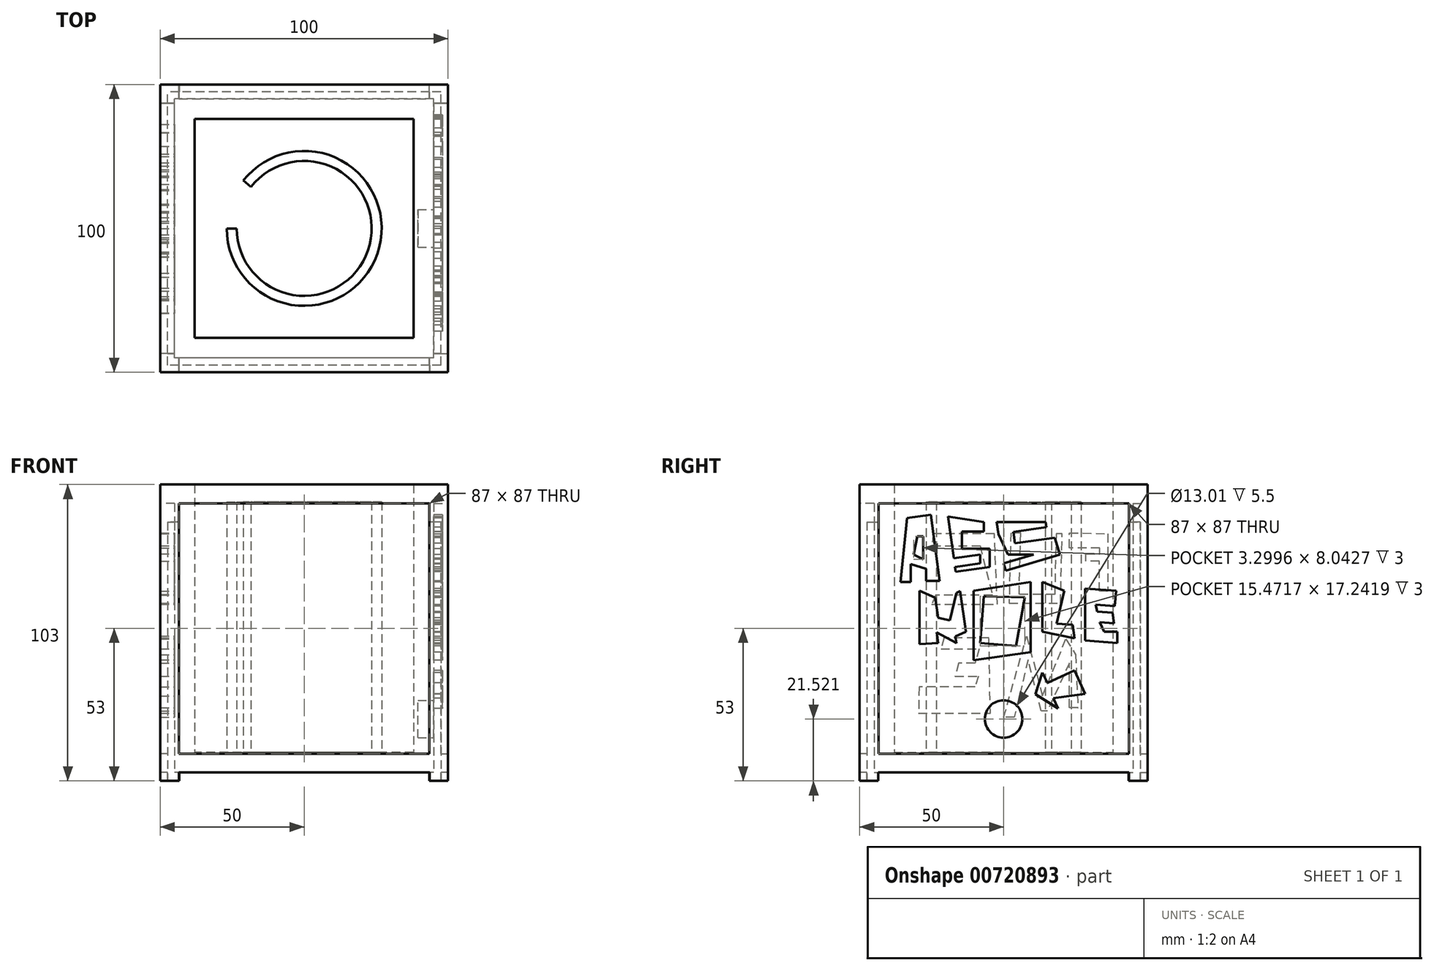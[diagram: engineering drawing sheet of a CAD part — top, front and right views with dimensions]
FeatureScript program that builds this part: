
annotation { "Feature Type Name" : "Feature", "Feature Type Description" : "" }
export const myFeature = defineFeature(function(context is Context, id is Id, definition is map)
    precondition{}
    {
        {
            var Q0;
            Q0=qCreatedBy(makeId("Top.planeOp"),FACE);
            var sketch = newSketch(context, id + "F0", { "sketchPlane" : qUnion([Q0])});
            skLineSegment(sketch, "E0.bottom", {"start": v(50, 50) * mm, "end": v(-50, 50) * mm});
            skLineSegment(sketch, "E0.top", {"start": v(50, -50) * mm, "end": v(-50, -50) * mm});
            skLineSegment(sketch, "E0.left", {"start": v(50, 50) * mm, "end": v(50, -50) * mm});
            skLineSegment(sketch, "E0.right", {"start": v(-50, 50) * mm, "end": v(-50, -50) * mm});
            skPoint(sketch, "E0.middle", {"position": v(0, 0) * mm});
            skSolve(sketch);
        }
        {
            var Q0;
            Q0=makeQuery(id+"F0.imprint","IMPRINT",FACE,{"disambiguationData":[TD([[makeQuery(id+"F0.imprint","IMPRINT",EDGE,{"derivedFrom":sQuery(id+"F0.wireOp",EDGE,"E0.bottom")}),1.0]])]});
            extrude(context, id + "F1", {"entities" : qUnion([Q0]), "depth" : 100 * mm, "offsetDistance" : 25 * mm});
        }
        {
            var Q0;
            Q0=makeQuery(id+"F1.opExtrude","CAP_FACE",FACE,{"disambiguationData":[OSD([sQuery(id+"F0.wireOp",EDGE,"E0.bottom"),sQuery(id+"F0.wireOp",EDGE,"E0.top"),sQuery(id+"F0.wireOp",EDGE,"E0.left"),sQuery(id+"F0.wireOp",EDGE,"E0.right")])],"isStart":true});
            var sketch = newSketch(context, id + "F2", { "sketchPlane" : qUnion([Q0])});
            skLineSegment(sketch, "E1.bottom", {"start": v(47.5, 47.5) * mm, "end": v(-47.5, 47.5) * mm});
            skLineSegment(sketch, "E1.top", {"start": v(47.5, -47.5) * mm, "end": v(-47.5, -47.5) * mm});
            skLineSegment(sketch, "E1.left", {"start": v(47.5, 47.5) * mm, "end": v(47.5, -47.5) * mm});
            skLineSegment(sketch, "E1.right", {"start": v(-47.5, 47.5) * mm, "end": v(-47.5, -47.5) * mm});
            skPoint(sketch, "E1.middle", {"position": v(0, 0) * mm});
            skLineSegment(sketch, "E2.bottom", {"start": v(45, 45) * mm, "end": v(-45, 45) * mm});
            skLineSegment(sketch, "E2.top", {"start": v(45, -45) * mm, "end": v(-45, -45) * mm});
            skLineSegment(sketch, "E2.left", {"start": v(45, 45) * mm, "end": v(45, -45) * mm});
            skLineSegment(sketch, "E2.right", {"start": v(-45, 45) * mm, "end": v(-45, -45) * mm});
            skSolve(sketch);
        }
        {
            var Q0;
            Q0=makeQuery(id+"F2.imprint","IMPRINT",FACE,{"disambiguationData":[TD([[makeQuery(id+"F2.imprint","IMPRINT",EDGE,{"derivedFrom":sQuery(id+"F2.wireOp",EDGE,"E1.bottom")}),1.0]])]});
            extrude(context, id + "F3", {"entities" : qUnion([Q0]), "operationType" : NewBodyOperationType.REMOVE, "oppositeDirection" : true, "depth" : 87 * mm, "offsetDistance" : 25 * mm});
        }
        {
            var Q0;
            Q0=makeQuery(id+"F1.opExtrude","CAP_FACE",FACE,{"disambiguationData":[OSD([sQuery(id+"F0.wireOp",EDGE,"E0.bottom"),sQuery(id+"F0.wireOp",EDGE,"E0.top"),sQuery(id+"F0.wireOp",EDGE,"E0.left"),sQuery(id+"F0.wireOp",EDGE,"E0.right")])],"isStart":false});
            shell(context, id + "F4", {"entities" : qUnion([Q0]), "thickness" : 7 * mm});
        }
        {
            var Q0;
            Q0=makeQuery(id+"F1.opExtrude","SWEPT_FACE",FACE,{"disambiguationData":[OSD([sQuery(id+"F0.wireOp",EDGE,"E0.right")])]});
            var sketch = newSketch(context, id + "F5", { "sketchPlane" : qUnion([Q0])});
            skLineSegment(sketch, "E3", {"start": v(0, 0) * mm, "end": v(0, 102.86) * mm, "construction": true});
            skLineSegment(sketch, "E4", {"start": v(-50, 50) * mm, "end": v(50, 50) * mm, "construction": true});
            skLineSegment(sketch, "E5.bottom", {"start": v(43.5, 93.5) * mm, "end": v(-43.5, 93.5) * mm});
            skLineSegment(sketch, "E5.top", {"start": v(43.5, 6.5) * mm, "end": v(-43.5, 6.5) * mm});
            skLineSegment(sketch, "E5.left", {"start": v(43.5, 93.5) * mm, "end": v(43.5, 6.5) * mm});
            skLineSegment(sketch, "E5.right", {"start": v(-43.5, 93.5) * mm, "end": v(-43.5, 6.5) * mm});
            skPoint(sketch, "E5.middle", {"position": v(0, 50) * mm});
            skSolve(sketch);
        }
        {
            var Q0;
            Q0=makeQuery(id+"F1.opExtrude","SWEPT_FACE",FACE,{"disambiguationData":[OSD([sQuery(id+"F0.wireOp",EDGE,"E0.top")])]});
            var sketch = newSketch(context, id + "F6", { "sketchPlane" : qUnion([Q0])});
            skLineSegment(sketch, "E6", {"start": v(-50, 50) * mm, "end": v(50, 50) * mm, "construction": true});
            skLineSegment(sketch, "E7", {"start": v(0, 0) * mm, "end": v(0, 100) * mm, "construction": true});
            skLineSegment(sketch, "E8.bottom", {"start": v(43.5, 93.5) * mm, "end": v(-43.5, 93.5) * mm});
            skLineSegment(sketch, "E8.top", {"start": v(43.5, 6.5) * mm, "end": v(-43.5, 6.5) * mm});
            skLineSegment(sketch, "E8.left", {"start": v(43.5, 93.5) * mm, "end": v(43.5, 6.5) * mm});
            skLineSegment(sketch, "E8.right", {"start": v(-43.5, 93.5) * mm, "end": v(-43.5, 6.5) * mm});
            skPoint(sketch, "E8.middle", {"position": v(0, 50) * mm});
            skSolve(sketch);
        }
        {
            var Q0;
            Q0=makeQuery(id+"F1.opExtrude","SWEPT_FACE",FACE,{"disambiguationData":[OSD([sQuery(id+"F0.wireOp",EDGE,"E0.left")])]});
            var sketch = newSketch(context, id + "F7", { "sketchPlane" : qUnion([Q0])});
            skLineSegment(sketch, "E9", {"start": v(-50, 50) * mm, "end": v(50, 50) * mm, "construction": true});
            skLineSegment(sketch, "E10", {"start": v(0, 100) * mm, "end": v(0, 0) * mm, "construction": true});
            skLineSegment(sketch, "E11.bottom", {"start": v(43.5, 93.5) * mm, "end": v(-43.5, 93.5) * mm});
            skLineSegment(sketch, "E11.top", {"start": v(43.5, 6.5) * mm, "end": v(-43.5, 6.5) * mm});
            skLineSegment(sketch, "E11.left", {"start": v(43.5, 93.5) * mm, "end": v(43.5, 6.5) * mm});
            skLineSegment(sketch, "E11.right", {"start": v(-43.5, 93.5) * mm, "end": v(-43.5, 6.5) * mm});
            skPoint(sketch, "E11.middle", {"position": v(0, 50) * mm});
            skSolve(sketch);
        }
        {
            var Q0;
            Q0=makeQuery(id+"F1.opExtrude","SWEPT_FACE",FACE,{"disambiguationData":[OSD([sQuery(id+"F0.wireOp",EDGE,"E0.bottom")])]});
            var sketch = newSketch(context, id + "F8", { "sketchPlane" : qUnion([Q0])});
            skLineSegment(sketch, "E12", {"start": v(-50, 50) * mm, "end": v(50, 50) * mm, "construction": true});
            skLineSegment(sketch, "E13", {"start": v(0, 100) * mm, "end": v(0, 0) * mm, "construction": true});
            skLineSegment(sketch, "E14.bottom", {"start": v(43.5, 93.5) * mm, "end": v(-43.5, 93.5) * mm});
            skLineSegment(sketch, "E14.top", {"start": v(43.5, 6.5) * mm, "end": v(-43.5, 6.5) * mm});
            skLineSegment(sketch, "E14.left", {"start": v(43.5, 93.5) * mm, "end": v(43.5, 6.5) * mm});
            skLineSegment(sketch, "E14.right", {"start": v(-43.5, 93.5) * mm, "end": v(-43.5, 6.5) * mm});
            skPoint(sketch, "E14.middle", {"position": v(0, 50) * mm});
            skSolve(sketch);
        }
        {
            var Q0;
            Q0=makeQuery(id+"F5.imprint","IMPRINT",FACE,{"disambiguationData":[TD([[makeQuery(id+"F5.imprint","IMPRINT",EDGE,{"derivedFrom":sQuery(id+"F5.wireOp",EDGE,"E5.bottom")}),1.0]])]});
            extrude(context, id + "F9", {"entities" : qUnion([Q0]), "operationType" : NewBodyOperationType.REMOVE, "oppositeDirection" : true, "depth" : 5 * mm, "offsetDistance" : 25 * mm});
        }
        {
            var Q0;
            Q0=makeQuery(id+"F7.imprint","IMPRINT",FACE,{"disambiguationData":[TD([[makeQuery(id+"F7.imprint","IMPRINT",EDGE,{"derivedFrom":sQuery(id+"F7.wireOp",EDGE,"E11.bottom")}),1.0]])]});
            extrude(context, id + "F10", {"entities" : qUnion([Q0]), "operationType" : NewBodyOperationType.REMOVE, "oppositeDirection" : true, "depth" : 5 * mm, "offsetDistance" : 25 * mm});
        }
        {
            var Q0;
            Q0=makeQuery(id+"F8.imprint","IMPRINT",FACE,{"disambiguationData":[TD([[makeQuery(id+"F8.imprint","IMPRINT",EDGE,{"derivedFrom":sQuery(id+"F8.wireOp",EDGE,"E14.bottom")}),1.0]])]});
            extrude(context, id + "F11", {"entities" : qUnion([Q0]), "operationType" : NewBodyOperationType.REMOVE, "oppositeDirection" : true, "depth" : 5 * mm, "offsetDistance" : 25 * mm});
        }
        {
            var Q0;
            Q0=makeQuery(id+"F6.imprint","IMPRINT",FACE,{"disambiguationData":[TD([[makeQuery(id+"F6.imprint","IMPRINT",EDGE,{"derivedFrom":sQuery(id+"F6.wireOp",EDGE,"E8.bottom")}),1.0]])]});
            extrude(context, id + "F12", {"entities" : qUnion([Q0]), "operationType" : NewBodyOperationType.REMOVE, "oppositeDirection" : true, "depth" : 5 * mm, "offsetDistance" : 25 * mm});
        }
        {
            var Q0;
            {var subQ0=sQuery(id+"F0.wireOp",EDGE,"E0.left");var subQ1=sQuery(id+"F0.wireOp",EDGE,"E0.top");var subQ2=sQuery(id+"F0.wireOp",EDGE,"E0.right");var subQ3=sQuery(id+"F0.wireOp",EDGE,"E0.bottom");Q0=makeQuery(id+"F3.boolean.opBoolean","SPLIT",FACE,{"disambiguationData":[TD([makeQuery(id+"F1.opExtrude","SWEPT_FACE",FACE,{"disambiguationData":[OSD([subQ3])]})])],"derivedFrom":makeQuery(id+"F1.opExtrude","CAP_FACE",FACE,{"disambiguationData":[OSD([subQ3,subQ1,subQ0,subQ2])],"isStart":true})});}
            var sketch = newSketch(context, id + "F13", { "sketchPlane" : qUnion([Q0])});
            skLineSegment(sketch, "E15", {"start": v(-47.5, 43.53) * mm, "end": v(-50, 43.53) * mm});
            skLineSegment(sketch, "E16", {"start": v(-50, 43.53) * mm, "end": v(-50, 50) * mm});
            skLineSegment(sketch, "E17", {"start": v(-50, 50) * mm, "end": v(-43.53, 50) * mm});
            skLineSegment(sketch, "E18", {"start": v(-43.53, 50) * mm, "end": v(-43.53, 47.5) * mm});
            skLineSegment(sketch, "E19", {"start": v(-43.53, 47.5) * mm, "end": v(-47.5, 47.5) * mm});
            skLineSegment(sketch, "E20", {"start": v(-47.5, 47.5) * mm, "end": v(-47.5, 43.53) * mm});
            skLineSegment(sketch, "E21", {"start": v(-47.5, -43.38) * mm, "end": v(-50, -43.38) * mm});
            skLineSegment(sketch, "E22", {"start": v(-50, -43.38) * mm, "end": v(-50, -50) * mm});
            skLineSegment(sketch, "E23", {"start": v(-50, -50) * mm, "end": v(-43.38, -50) * mm});
            skLineSegment(sketch, "E24", {"start": v(-43.38, -50) * mm, "end": v(-43.38, -47.5) * mm});
            skLineSegment(sketch, "E25", {"start": v(-43.38, -47.5) * mm, "end": v(-47.5, -47.5) * mm});
            skLineSegment(sketch, "E26", {"start": v(-47.5, -47.5) * mm, "end": v(-47.5, -43.38) * mm});
            skLineSegment(sketch, "E27", {"start": v(43.51, -47.5) * mm, "end": v(43.51, -50) * mm});
            skLineSegment(sketch, "E28", {"start": v(43.51, -50) * mm, "end": v(50, -50) * mm});
            skLineSegment(sketch, "E29", {"start": v(50, -50) * mm, "end": v(50, -43.51) * mm});
            skLineSegment(sketch, "E30", {"start": v(50, -43.51) * mm, "end": v(47.5, -43.51) * mm});
            skLineSegment(sketch, "E31", {"start": v(47.5, -43.51) * mm, "end": v(47.5, -47.5) * mm});
            skLineSegment(sketch, "E32", {"start": v(47.5, -47.5) * mm, "end": v(43.51, -47.5) * mm});
            skLineSegment(sketch, "E33", {"start": v(43.58, 47.5) * mm, "end": v(43.58, 50) * mm});
            skLineSegment(sketch, "E34", {"start": v(43.58, 50) * mm, "end": v(50, 50) * mm});
            skLineSegment(sketch, "E35", {"start": v(50, 50) * mm, "end": v(50, 43.58) * mm});
            skLineSegment(sketch, "E36", {"start": v(50, 43.58) * mm, "end": v(47.5, 43.58) * mm});
            skLineSegment(sketch, "E37", {"start": v(47.5, 43.58) * mm, "end": v(47.5, 47.5) * mm});
            skLineSegment(sketch, "E38", {"start": v(47.5, 47.5) * mm, "end": v(43.58, 47.5) * mm});
            skSolve(sketch);
        }
        {
            var Q0;
            Q0=makeQuery(id+"F13.imprint","IMPRINT",FACE,{"disambiguationData":[TD([[makeQuery(id+"F13.imprint","IMPRINT",EDGE,{"derivedFrom":sQuery(id+"F13.wireOp",EDGE,"E27")}),1.0]])]});
            var Q1;
            Q1=makeQuery(id+"F13.imprint","IMPRINT",FACE,{"disambiguationData":[TD([[makeQuery(id+"F13.imprint","IMPRINT",EDGE,{"derivedFrom":sQuery(id+"F13.wireOp",EDGE,"E21")}),1.0]])]});
            var Q2;
            Q2=makeQuery(id+"F13.imprint","IMPRINT",FACE,{"disambiguationData":[TD([[makeQuery(id+"F13.imprint","IMPRINT",EDGE,{"derivedFrom":sQuery(id+"F13.wireOp",EDGE,"E15")}),-1.0]])]});
            var Q3;
            Q3=makeQuery(id+"F13.imprint","IMPRINT",FACE,{"disambiguationData":[TD([[makeQuery(id+"F13.imprint","IMPRINT",EDGE,{"derivedFrom":sQuery(id+"F13.wireOp",EDGE,"E33")}),-1.0]])]});
            extrude(context, id + "F14", {"entities" : qUnion([Q0, Q1, Q2, Q3]), "operationType" : NewBodyOperationType.ADD, "depth" : 3 * mm, "offsetDistance" : 25 * mm});
        }
        {
            var Q0;
            Q0=makeQuery(id+"F4.opShell","OFFSET_FACE",FACE,{"disambiguationData":[OSD([sQuery(id+"F0.wireOp",EDGE,"E0.bottom"),sQuery(id+"F0.wireOp",EDGE,"E0.top"),sQuery(id+"F0.wireOp",EDGE,"E0.left"),sQuery(id+"F0.wireOp",EDGE,"E0.right")])]});
            var sketch = newSketch(context, id + "F15", { "sketchPlane" : qUnion([Q0])});
            skArc(sketch, "E39", {"start": v(-23.44, 0) * mm, "mid": v(22.16, -7.63) * mm, "end": v(-18.47, 14.42) * mm});
            skLineSegment(sketch, "E40", {"start": v(-26.91, 0) * mm, "end": v(-23.44, 0) * mm});
            skLineSegment(sketch, "E41", {"start": v(-21.13, 16.67) * mm, "end": v(-18.47, 14.42) * mm});
            skArc(sketch, "E42", {"start": v(-21.13, 16.67) * mm, "mid": v(25.42, -8.82) * mm, "end": v(-26.91, 0) * mm});
            skSolve(sketch);
        }
        {
            var Q0;
            Q0 = qSketchRegion(id + "F15", true);
            extrude(context, id + "F16", {"entities" : qUnion([Q0]), "operationType" : NewBodyOperationType.ADD, "depth" : 87 * mm, "offsetDistance" : 25 * mm});
        }
        {
            var Q0;
            Q0=makeQuery(id+"F4.opShell","OFFSET_FACE",FACE,{"disambiguationData":[OSD([sQuery(id+"F2.wireOp",EDGE,"E1.bottom"),sQuery(id+"F2.wireOp",EDGE,"E1.top"),sQuery(id+"F2.wireOp",EDGE,"E1.left"),sQuery(id+"F2.wireOp",EDGE,"E1.right"),sQuery(id+"F2.wireOp",EDGE,"E2.bottom"),sQuery(id+"F2.wireOp",EDGE,"E2.top"),sQuery(id+"F2.wireOp",EDGE,"E2.left"),sQuery(id+"F2.wireOp",EDGE,"E2.right")])]});
            extrude(context, id + "F17", {"entities" : qUnion([Q0]), "operationType" : NewBodyOperationType.ADD, "depth" : 6 * mm, "offsetDistance" : 25 * mm});
        }
        {
            var Q0;
            Q0=makeQuery(id+"F9.boolean.opBoolean","MERGE",FACE,{"derivedFrom":[makeQuery(id+"F3.boolean.opBoolean","COPY",FACE,{"derivedFrom":makeQuery(id+"F3.opExtrude","SWEPT_FACE",FACE,{"disambiguationData":[OSD([sQuery(id+"F2.wireOp",EDGE,"E2.right")])]})}),makeQuery(id+"F9.opExtrude","CAP_FACE",FACE,{"disambiguationData":[OSD([sQuery(id+"F5.wireOp",EDGE,"E5.bottom"),sQuery(id+"F5.wireOp",EDGE,"E5.top"),sQuery(id+"F5.wireOp",EDGE,"E5.left"),sQuery(id+"F5.wireOp",EDGE,"E5.right")])],"isStart":false})]});
            var sketch = newSketch(context, id + "F18", { "sketchPlane" : qUnion([Q0])});
            skLineSegment(sketch, "E43", {"start": v(-36.15, 82.9) * mm, "end": v(-36.15, 62.97) * mm});
            skLineSegment(sketch, "E44", {"start": v(-36.15, 62.97) * mm, "end": v(-33.22, 62.97) * mm});
            skLineSegment(sketch, "E45", {"start": v(-33.22, 62.97) * mm, "end": v(-33.22, 73.32) * mm});
            skLineSegment(sketch, "E46", {"start": v(-33.22, 73.32) * mm, "end": v(-28.58, 73.32) * mm});
            skLineSegment(sketch, "E47", {"start": v(-28.58, 73.32) * mm, "end": v(-28.58, 75.95) * mm});
            skLineSegment(sketch, "E48", {"start": v(-28.58, 75.95) * mm, "end": v(-33.37, 75.95) * mm});
            skLineSegment(sketch, "E49", {"start": v(-33.37, 75.95) * mm, "end": v(-33.37, 77.96) * mm});
            skLineSegment(sketch, "E50", {"start": v(-33.37, 77.96) * mm, "end": v(-22.86, 77.96) * mm});
            skLineSegment(sketch, "E51", {"start": v(-22.86, 77.96) * mm, "end": v(-22.86, 83.21) * mm});
            skLineSegment(sketch, "E52", {"start": v(-22.86, 83.21) * mm, "end": v(-36.15, 82.9) * mm});
            skLineSegment(sketch, "E53", {"start": v(-18.23, 82.9) * mm, "end": v(-17.74, 61.88) * mm});
            skLineSegment(sketch, "E54", {"start": v(-17.74, 61.88) * mm, "end": v(-5.4, 61.88) * mm});
            skLineSegment(sketch, "E55", {"start": v(-5.4, 61.88) * mm, "end": v(-5.9, 83.21) * mm});
            skLineSegment(sketch, "E56", {"start": v(-5.9, 83.21) * mm, "end": v(-2.47, 83.21) * mm});
            skLineSegment(sketch, "E57", {"start": v(-2.47, 83.21) * mm, "end": v(-1.9, 58.82) * mm});
            skLineSegment(sketch, "E58", {"start": v(-1.9, 58.82) * mm, "end": v(-19.77, 58.82) * mm});
            skLineSegment(sketch, "E59", {"start": v(-19.77, 58.82) * mm, "end": v(-20.34, 82.9) * mm});
            skLineSegment(sketch, "E60", {"start": v(-20.34, 82.9) * mm, "end": v(-18.23, 82.9) * mm});
            skLineSegment(sketch, "E61", {"start": v(3.24, 82.9) * mm, "end": v(24.4, 82.9) * mm});
            skLineSegment(sketch, "E62", {"start": v(24.4, 82.9) * mm, "end": v(24.87, 78.73) * mm});
            skLineSegment(sketch, "E63", {"start": v(24.87, 78.73) * mm, "end": v(8.19, 78.73) * mm});
            skLineSegment(sketch, "E64", {"start": v(8.19, 78.73) * mm, "end": v(3.86, 61.58) * mm});
            skLineSegment(sketch, "E65", {"start": v(3.86, 61.58) * mm, "end": v(23.64, 61.58) * mm});
            skLineSegment(sketch, "E66", {"start": v(23.64, 61.58) * mm, "end": v(25.03, 58.34) * mm});
            skLineSegment(sketch, "E67", {"start": v(25.03, 58.34) * mm, "end": v(2.16, 58.34) * mm});
            skLineSegment(sketch, "E68", {"start": v(2.16, 58.34) * mm, "end": v(3.24, 82.9) * mm});
            skLineSegment(sketch, "E69", {"start": v(-25.03, 40.88) * mm, "end": v(-25.84, 22.47) * mm});
            skLineSegment(sketch, "E70", {"start": v(-25.84, 22.47) * mm, "end": v(-22.86, 22.47) * mm});
            skLineSegment(sketch, "E71", {"start": v(-22.86, 22.47) * mm, "end": v(-22.86, 37.94) * mm});
            skLineSegment(sketch, "E72", {"start": v(-22.86, 37.94) * mm, "end": v(-15.3, 21.26) * mm});
            skLineSegment(sketch, "E73", {"start": v(-15.3, 21.26) * mm, "end": v(-13.13, 21.26) * mm});
            skLineSegment(sketch, "E74", {"start": v(-13.13, 21.26) * mm, "end": v(-8.5, 39.03) * mm});
            skLineSegment(sketch, "E75", {"start": v(-8.5, 39.03) * mm, "end": v(-3.7, 19.1) * mm});
            skLineSegment(sketch, "E76", {"start": v(-3.7, 19.1) * mm, "end": v(0, 19.1) * mm});
            skLineSegment(sketch, "E77", {"start": v(0, 19.1) * mm, "end": v(-8.03, 47.37) * mm});
            skLineSegment(sketch, "E78", {"start": v(-8.03, 47.37) * mm, "end": v(-13.48, 26.48) * mm});
            skLineSegment(sketch, "E79", {"start": v(-13.48, 26.48) * mm, "end": v(-21.63, 46.29) * mm});
            skLineSegment(sketch, "E80", {"start": v(-21.63, 46.29) * mm, "end": v(-25.03, 40.88) * mm});
            skLineSegment(sketch, "E81", {"start": v(5.1, 46.75) * mm, "end": v(20.7, 46.75) * mm});
            skLineSegment(sketch, "E82", {"start": v(20.7, 46.75) * mm, "end": v(21.78, 42.95) * mm});
            skLineSegment(sketch, "E83", {"start": v(21.78, 42.95) * mm, "end": v(8.5, 42.95) * mm});
            skLineSegment(sketch, "E84", {"start": v(8.5, 42.95) * mm, "end": v(9.92, 37.93) * mm});
            skLineSegment(sketch, "E85", {"start": v(9.92, 37.93) * mm, "end": v(15.6, 37.93) * mm});
            skLineSegment(sketch, "E86", {"start": v(15.6, 37.93) * mm, "end": v(16.89, 33.41) * mm});
            skLineSegment(sketch, "E87", {"start": v(16.89, 33.41) * mm, "end": v(8.8, 33.41) * mm});
            skLineSegment(sketch, "E88", {"start": v(8.8, 33.41) * mm, "end": v(9.87, 29.68) * mm});
            skLineSegment(sketch, "E89", {"start": v(9.87, 29.68) * mm, "end": v(29.35, 29.68) * mm});
            skLineSegment(sketch, "E90", {"start": v(29.35, 29.68) * mm, "end": v(29.57, 20.5) * mm});
            skLineSegment(sketch, "E91", {"start": v(29.57, 20.5) * mm, "end": v(4.63, 20.5) * mm});
            skLineSegment(sketch, "E92", {"start": v(4.63, 20.5) * mm, "end": v(5.1, 46.75) * mm});
            skSolve(sketch);
        }
        {
            var Q0;
            Q0=makeQuery(id+"F18.imprint","IMPRINT",FACE,{"disambiguationData":[TD([[makeQuery(id+"F18.imprint","IMPRINT",EDGE,{"derivedFrom":sQuery(id+"F18.wireOp",EDGE,"E43")}),1.0]])]});
            var Q1;
            Q1=makeQuery(id+"F18.imprint","IMPRINT",FACE,{"disambiguationData":[TD([[makeQuery(id+"F18.imprint","IMPRINT",EDGE,{"derivedFrom":sQuery(id+"F18.wireOp",EDGE,"E53")}),-1.0]])]});
            var Q2;
            Q2=makeQuery(id+"F18.imprint","IMPRINT",FACE,{"disambiguationData":[TD([[makeQuery(id+"F18.imprint","IMPRINT",EDGE,{"derivedFrom":sQuery(id+"F18.wireOp",EDGE,"E61")}),-1.0]])]});
            var Q3;
            Q3=makeQuery(id+"F18.imprint","IMPRINT",FACE,{"disambiguationData":[TD([[makeQuery(id+"F18.imprint","IMPRINT",EDGE,{"derivedFrom":sQuery(id+"F18.wireOp",EDGE,"E69")}),1.0]])]});
            var Q4;
            Q4=makeQuery(id+"F18.imprint","IMPRINT",FACE,{"disambiguationData":[TD([[makeQuery(id+"F18.imprint","IMPRINT",EDGE,{"derivedFrom":sQuery(id+"F18.wireOp",EDGE,"E81")}),-1.0]])]});
            extrude(context, id + "F19", {"entities" : qUnion([Q0, Q1, Q2, Q3, Q4]), "operationType" : NewBodyOperationType.ADD, "depth" : 5 * mm, "offsetDistance" : 25 * mm});
        }
        {
            var Q0;
            Q0=makeQuery(id+"F10.boolean.opBoolean","MERGE",FACE,{"derivedFrom":[makeQuery(id+"F3.boolean.opBoolean","COPY",FACE,{"derivedFrom":makeQuery(id+"F3.opExtrude","SWEPT_FACE",FACE,{"disambiguationData":[OSD([sQuery(id+"F2.wireOp",EDGE,"E2.left")])]})}),makeQuery(id+"F10.opExtrude","CAP_FACE",FACE,{"disambiguationData":[OSD([sQuery(id+"F7.wireOp",EDGE,"E11.bottom"),sQuery(id+"F7.wireOp",EDGE,"E11.top"),sQuery(id+"F7.wireOp",EDGE,"E11.left"),sQuery(id+"F7.wireOp",EDGE,"E11.right")])],"isStart":false})]});
            var sketch = newSketch(context, id + "F20", { "sketchPlane" : qUnion([Q0])});
            skCircle(sketch, "E93", {"center": v(0, 18.73) * mm, "radius": 6.3 * mm});
            skLineSegment(sketch, "E94", {"start": v(-35.79, 66.16) * mm, "end": v(-32.28, 66.16) * mm});
            skLineSegment(sketch, "E95", {"start": v(-32.28, 66.16) * mm, "end": v(-32.28, 72.34) * mm});
            skLineSegment(sketch, "E96", {"start": v(-32.28, 72.34) * mm, "end": v(-26.92, 70.7) * mm});
            skLineSegment(sketch, "E97", {"start": v(-26.92, 70.7) * mm, "end": v(-26.92, 66.57) * mm});
            skLineSegment(sketch, "E98", {"start": v(-26.92, 66.57) * mm, "end": v(-22.18, 66.57) * mm});
            skLineSegment(sketch, "E99", {"start": v(-22.18, 66.57) * mm, "end": v(-25.27, 89.46) * mm});
            skLineSegment(sketch, "E100", {"start": v(-25.27, 89.46) * mm, "end": v(-33.6, 88.34) * mm});
            skLineSegment(sketch, "E101", {"start": v(-33.6, 88.34) * mm, "end": v(-35.79, 66.16) * mm});
            skLineSegment(sketch, "E102", {"start": v(-31.25, 75.64) * mm, "end": v(-27.95, 74) * mm});
            skLineSegment(sketch, "E103", {"start": v(-27.95, 74) * mm, "end": v(-27.95, 82.04) * mm});
            skLineSegment(sketch, "E104", {"start": v(-27.95, 82.04) * mm, "end": v(-30.01, 82.04) * mm});
            skLineSegment(sketch, "E105", {"start": v(-30.01, 82.04) * mm, "end": v(-31.25, 75.64) * mm});
            skLineSegment(sketch, "E106", {"start": v(-6.92, 87) * mm, "end": v(-6.92, 83.69) * mm});
            skLineSegment(sketch, "E107", {"start": v(-6.92, 83.69) * mm, "end": v(-14.55, 83.69) * mm});
            skLineSegment(sketch, "E108", {"start": v(-14.55, 83.69) * mm, "end": v(-14.55, 77.7) * mm});
            skLineSegment(sketch, "E109", {"start": v(-14.55, 77.7) * mm, "end": v(-4.86, 77.7) * mm});
            skLineSegment(sketch, "E110", {"start": v(-4.86, 77.7) * mm, "end": v(-4.86, 71.31) * mm});
            skLineSegment(sketch, "E111", {"start": v(-4.86, 71.31) * mm, "end": v(-16.61, 69.66) * mm});
            skLineSegment(sketch, "E112", {"start": v(-16.61, 69.66) * mm, "end": v(-16.85, 71.37) * mm});
            skLineSegment(sketch, "E113", {"start": v(-16.85, 71.37) * mm, "end": v(-8.16, 72.59) * mm});
            skLineSegment(sketch, "E114", {"start": v(-8.16, 72.59) * mm, "end": v(-8.16, 75.64) * mm});
            skLineSegment(sketch, "E115", {"start": v(-8.16, 75.64) * mm, "end": v(-17.26, 74.37) * mm});
            skLineSegment(sketch, "E116", {"start": v(-17.26, 74.37) * mm, "end": v(-19.29, 88.85) * mm});
            skLineSegment(sketch, "E117", {"start": v(-19.29, 88.85) * mm, "end": v(-6.92, 87) * mm});
            skLineSegment(sketch, "E118", {"start": v(-2.38, 87) * mm, "end": v(-1.8, 82.8) * mm});
            skLineSegment(sketch, "E119", {"start": v(-1.8, 82.8) * mm, "end": v(1.54, 75.64) * mm});
            skLineSegment(sketch, "E120", {"start": v(1.54, 75.64) * mm, "end": v(10.4, 75.64) * mm});
            skLineSegment(sketch, "E121", {"start": v(10.4, 75.64) * mm, "end": v(0, 72.59) * mm});
            skLineSegment(sketch, "E122", {"start": v(0, 72.59) * mm, "end": v(0.73, 70.12) * mm});
            skLineSegment(sketch, "E123", {"start": v(0.73, 70.12) * mm, "end": v(19.54, 75.64) * mm});
            skLineSegment(sketch, "E124", {"start": v(19.54, 75.64) * mm, "end": v(17.8, 81.53) * mm});
            skLineSegment(sketch, "E125", {"start": v(17.8, 81.53) * mm, "end": v(3.92, 79.58) * mm});
            skLineSegment(sketch, "E126", {"start": v(3.92, 79.58) * mm, "end": v(3.36, 83.57) * mm});
            skLineSegment(sketch, "E127", {"start": v(3.36, 83.57) * mm, "end": v(14.85, 85.18) * mm});
            skLineSegment(sketch, "E128", {"start": v(14.85, 85.18) * mm, "end": v(14.6, 87) * mm});
            skLineSegment(sketch, "E129", {"start": v(14.6, 87) * mm, "end": v(-2.38, 87) * mm});
            skLineSegment(sketch, "E130", {"start": v(-29.19, 63.06) * mm, "end": v(-29.19, 44.5) * mm});
            skLineSegment(sketch, "E131", {"start": v(-29.19, 44.5) * mm, "end": v(-22.8, 44.92) * mm});
            skLineSegment(sketch, "E132", {"start": v(-22.8, 44.92) * mm, "end": v(-23.3, 48.56) * mm});
            skLineSegment(sketch, "E133", {"start": v(-23.3, 48.56) * mm, "end": v(-16.4, 44.92) * mm});
            skLineSegment(sketch, "E134", {"start": v(-16.4, 44.92) * mm, "end": v(-16.72, 47.2) * mm});
            skLineSegment(sketch, "E135", {"start": v(-16.72, 47.2) * mm, "end": v(-13.1, 48.89) * mm});
            skLineSegment(sketch, "E136", {"start": v(-13.1, 48.89) * mm, "end": v(-15.08, 62.99) * mm});
            skLineSegment(sketch, "E137", {"start": v(-15.08, 62.99) * mm, "end": v(-16.4, 62.37) * mm});
            skLineSegment(sketch, "E138", {"start": v(-16.4, 62.37) * mm, "end": v(-18.67, 52.75) * mm});
            skLineSegment(sketch, "E139", {"start": v(-18.67, 52.75) * mm, "end": v(-22.72, 53.7) * mm});
            skLineSegment(sketch, "E140", {"start": v(-22.72, 53.7) * mm, "end": v(-23.7, 60.67) * mm});
            skLineSegment(sketch, "E141", {"start": v(-23.7, 60.67) * mm, "end": v(-29.19, 63.06) * mm});
            skLineSegment(sketch, "E142", {"start": v(-6.92, 61.2) * mm, "end": v(-8.16, 44.92) * mm});
            skLineSegment(sketch, "E143", {"start": v(-8.16, 44.92) * mm, "end": v(4.3, 43.97) * mm});
            skLineSegment(sketch, "E144", {"start": v(4.3, 43.97) * mm, "end": v(7.31, 60.8) * mm});
            skLineSegment(sketch, "E145", {"start": v(7.31, 60.8) * mm, "end": v(-6.92, 61.2) * mm});
            skLineSegment(sketch, "E146", {"start": v(-10.42, 63.06) * mm, "end": v(-10.42, 38.94) * mm});
            skLineSegment(sketch, "E147", {"start": v(-10.42, 38.94) * mm, "end": v(9.36, 41.71) * mm});
            skLineSegment(sketch, "E148", {"start": v(9.36, 41.71) * mm, "end": v(9.36, 66.16) * mm});
            skLineSegment(sketch, "E149", {"start": v(9.36, 66.16) * mm, "end": v(-10.42, 63.06) * mm});
            skLineSegment(sketch, "E150", {"start": v(13.5, 66.16) * mm, "end": v(13.5, 48.89) * mm});
            skLineSegment(sketch, "E151", {"start": v(13.5, 48.89) * mm, "end": v(24.63, 46.57) * mm});
            skLineSegment(sketch, "E152", {"start": v(24.63, 46.57) * mm, "end": v(23.98, 51.22) * mm});
            skLineSegment(sketch, "E153", {"start": v(23.98, 51.22) * mm, "end": v(18.47, 51.64) * mm});
            skLineSegment(sketch, "E154", {"start": v(18.47, 51.64) * mm, "end": v(21.13, 63.06) * mm});
            skLineSegment(sketch, "E155", {"start": v(21.13, 63.06) * mm, "end": v(13.5, 66.16) * mm});
            skLineSegment(sketch, "E156", {"start": v(28.35, 63.89) * mm, "end": v(39.16, 63.06) * mm});
            skLineSegment(sketch, "E157", {"start": v(39.16, 63.06) * mm, "end": v(38.66, 57.7) * mm});
            skLineSegment(sketch, "E158", {"start": v(38.66, 57.7) * mm, "end": v(31.97, 58.21) * mm});
            skLineSegment(sketch, "E159", {"start": v(31.97, 58.21) * mm, "end": v(32.47, 55.85) * mm});
            skLineSegment(sketch, "E160", {"start": v(32.47, 55.85) * mm, "end": v(37.88, 55.43) * mm});
            skLineSegment(sketch, "E161", {"start": v(37.88, 55.43) * mm, "end": v(38.39, 51.8) * mm});
            skLineSegment(sketch, "E162", {"start": v(38.39, 51.8) * mm, "end": v(33.33, 52.19) * mm});
            skLineSegment(sketch, "E163", {"start": v(33.33, 52.19) * mm, "end": v(34.87, 48.89) * mm});
            skLineSegment(sketch, "E164", {"start": v(34.87, 48.89) * mm, "end": v(39.48, 48.89) * mm});
            skLineSegment(sketch, "E165", {"start": v(39.48, 48.89) * mm, "end": v(39.48, 44.92) * mm});
            skLineSegment(sketch, "E166", {"start": v(39.48, 44.92) * mm, "end": v(28.35, 45.77) * mm});
            skLineSegment(sketch, "E167", {"start": v(28.35, 45.77) * mm, "end": v(28.35, 63.89) * mm});
            skLineSegment(sketch, "E168", {"start": v(24.63, 35.43) * mm, "end": v(15.17, 31.03) * mm});
            skLineSegment(sketch, "E169", {"start": v(15.17, 31.03) * mm, "end": v(13.5, 34.62) * mm});
            skLineSegment(sketch, "E170", {"start": v(13.5, 34.62) * mm, "end": v(11.02, 27.18) * mm});
            skLineSegment(sketch, "E171", {"start": v(11.02, 27.18) * mm, "end": v(18.86, 22.23) * mm});
            skLineSegment(sketch, "E172", {"start": v(18.86, 22.23) * mm, "end": v(17.22, 25.76) * mm});
            skLineSegment(sketch, "E173", {"start": v(17.22, 25.76) * mm, "end": v(28.35, 27.32) * mm});
            skLineSegment(sketch, "E174", {"start": v(28.35, 27.32) * mm, "end": v(24.63, 35.43) * mm});
            skSolve(sketch);
        }
        {
            var Q0;
            Q0=makeQuery(id+"F20.imprint","IMPRINT",FACE,{"disambiguationData":[TD([[makeQuery(id+"F20.imprint","IMPRINT",EDGE,{"derivedFrom":sQuery(id+"F20.wireOp",EDGE,"E94")}),1.0]])]});
            var Q1;
            Q1=makeQuery(id+"F20.imprint","IMPRINT",FACE,{"disambiguationData":[TD([[makeQuery(id+"F20.imprint","IMPRINT",EDGE,{"derivedFrom":sQuery(id+"F20.wireOp",EDGE,"E106")}),-1.0]])]});
            var Q2;
            Q2=makeQuery(id+"F20.imprint","IMPRINT",FACE,{"disambiguationData":[TD([[makeQuery(id+"F20.imprint","IMPRINT",EDGE,{"derivedFrom":sQuery(id+"F20.wireOp",EDGE,"E118")}),1.0]])]});
            var Q3;
            Q3=makeQuery(id+"F20.imprint","IMPRINT",FACE,{"disambiguationData":[TD([[makeQuery(id+"F20.imprint","IMPRINT",EDGE,{"derivedFrom":sQuery(id+"F20.wireOp",EDGE,"E130")}),1.0]])]});
            var Q4;
            Q4=makeQuery(id+"F20.imprint","IMPRINT",FACE,{"disambiguationData":[TD([[makeQuery(id+"F20.imprint","IMPRINT",EDGE,{"derivedFrom":sQuery(id+"F20.wireOp",EDGE,"E142")}),-1.0]])]});
            var Q5;
            Q5=makeQuery(id+"F20.imprint","IMPRINT",FACE,{"disambiguationData":[TD([[makeQuery(id+"F20.imprint","IMPRINT",EDGE,{"derivedFrom":sQuery(id+"F20.wireOp",EDGE,"E150")}),1.0]])]});
            var Q6;
            Q6=makeQuery(id+"F20.imprint","IMPRINT",FACE,{"disambiguationData":[TD([[makeQuery(id+"F20.imprint","IMPRINT",EDGE,{"derivedFrom":sQuery(id+"F20.wireOp",EDGE,"E156")}),-1.0]])]});
            var Q7;
            Q7=makeQuery(id+"F20.imprint","IMPRINT",FACE,{"disambiguationData":[TD([[makeQuery(id+"F20.imprint","IMPRINT",EDGE,{"derivedFrom":sQuery(id+"F20.wireOp",EDGE,"E168")}),1.0]])]});
            extrude(context, id + "F21", {"entities" : qUnion([Q0, Q1, Q2, Q3, Q4, Q5, Q6, Q7]), "operationType" : NewBodyOperationType.ADD, "depth" : 3 * mm, "offsetDistance" : 25 * mm});
        }
        {
            var Q0;
            {var subQ0=sQuery(id+"F2.wireOp",EDGE,"E2.left");var subQ2=sQuery(id+"F2.wireOp",EDGE,"E2.bottom");var subQ3=sQuery(id+"F7.wireOp",EDGE,"E11.left");var subQ4=sQuery(id+"F7.wireOp",EDGE,"E11.bottom");var subQ5=sQuery(id+"F7.wireOp",EDGE,"E11.right");Q0=makeQuery(id+"F21.boolean.opBoolean","SPLIT",FACE,{"disambiguationData":[TD([makeQuery(id+"F3.boolean.opBoolean","COPY",FACE,{"derivedFrom":makeQuery(id+"F3.opExtrude","SWEPT_FACE",FACE,{"disambiguationData":[OSD([subQ2])]})})])],"derivedFrom":makeQuery(id+"F10.boolean.opBoolean","MERGE",FACE,{"derivedFrom":[makeQuery(id+"F3.boolean.opBoolean","COPY",FACE,{"derivedFrom":makeQuery(id+"F3.opExtrude","SWEPT_FACE",FACE,{"disambiguationData":[OSD([subQ0])]})}),makeQuery(id+"F10.opExtrude","CAP_FACE",FACE,{"disambiguationData":[OSD([subQ4,sQuery(id+"F7.wireOp",EDGE,"E11.top"),subQ3,subQ5])],"isStart":false})]})});}
            var sketch = newSketch(context, id + "F22", { "sketchPlane" : qUnion([Q0])});
            skCircle(sketch, "E175", {"center": v(0, 18.52) * mm, "radius": 6.5 * mm});
            skSolve(sketch);
        }
        {
            var Q0;
            Q0=makeQuery(id+"F22.imprint","IMPRINT",FACE,{"disambiguationData":[TD([[makeQuery(id+"F22.imprint","IMPRINT",EDGE,{"derivedFrom":sQuery(id+"F22.wireOp",EDGE,"E175")}),1.0]])]});
            extrude(context, id + "F23", {"entities" : qUnion([Q0]), "operationType" : NewBodyOperationType.REMOVE, "oppositeDirection" : true, "depth" : 5.5 * mm, "offsetDistance" : 25 * mm});
        }
    });
